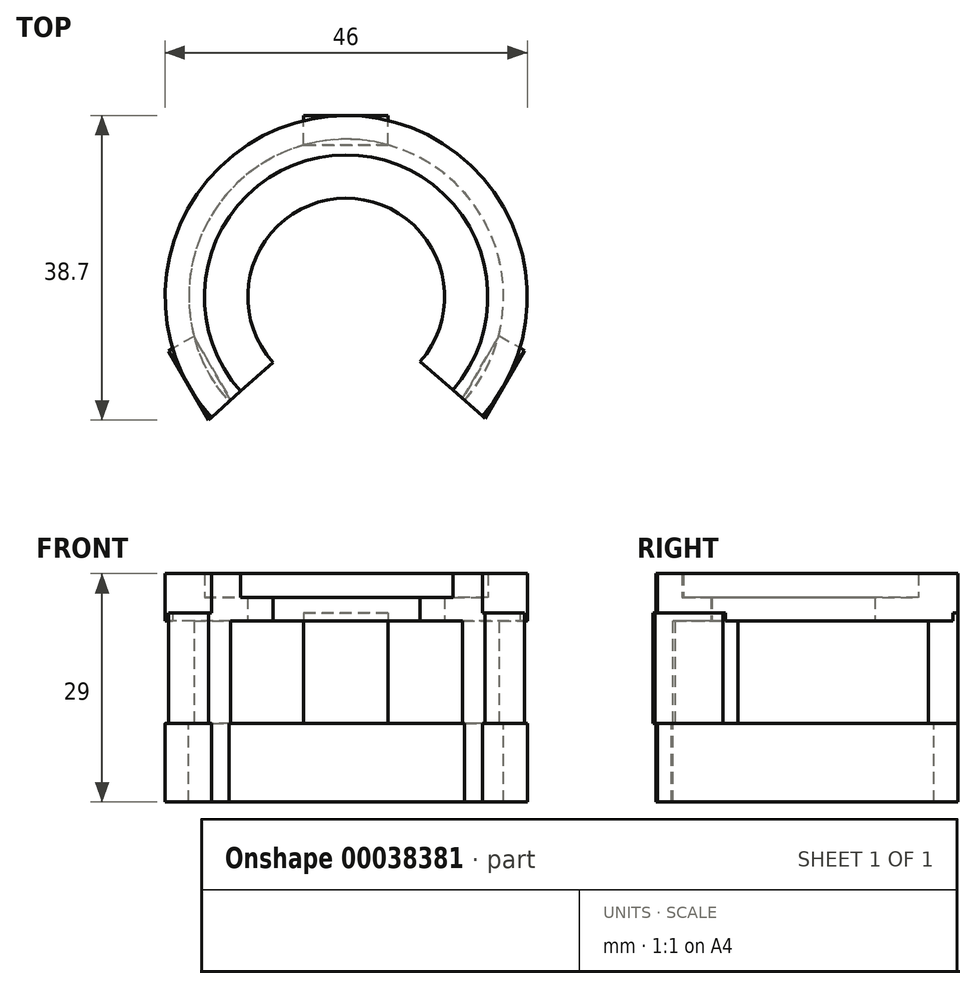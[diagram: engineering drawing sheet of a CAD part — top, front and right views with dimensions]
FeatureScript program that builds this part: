
annotation { "Feature Type Name" : "Feature", "Feature Type Description" : "" }
export const myFeature = defineFeature(function(context is Context, id is Id, definition is map)
    precondition{}
    {
        {
            var Q0;
            Q0=qCreatedBy(makeId("Top.planeOp"),FACE);
            var sketch = newSketch(context, id + "F0", { "sketchPlane" : qUnion([Q0])});
            skCircle(sketch, "E0", {"center": v(0, 0) * mm, "radius": 20 * mm});
            skCircle(sketch, "E1.0", {"center": v(0, 0) * mm, "radius": 23 * mm});
            skSolve(sketch);
        }
        {
            var Q0;
            Q0=makeQuery(id+"F0.imprint","IMPRINT",FACE,{"disambiguationData":[TD([[makeQuery(id+"F0.imprint","IMPRINT",EDGE,{"derivedFrom":sQuery(id+"F0.wireOp",EDGE,"E0")}),-1.0]])]});
            extrude(context, id + "F1", {"entities" : qUnion([Q0]), "oppositeDirection" : true, "depth" : 10 * mm});
        }
        {
            var Q0;
            Q0=qCreatedBy(makeId("Top.planeOp"),FACE);
            cPlane(context, id + "F2", {"entities" : qUnion([Q0]), "cplaneType" : CPlaneType.OFFSET, "offset" : 13 * mm, "width" : 150 * mm, "height" : 150 * mm});
        }
        {
            var Q0;
            Q0=qCreatedBy(id+"F2.planeOp",FACE);
            var sketch = newSketch(context, id + "F3", { "sketchPlane" : qUnion([Q0])});
            skCircle(sketch, "E2", {"center": v(0, 0) * mm, "radius": 18 * mm});
            skCircle(sketch, "E3", {"center": v(0, 0) * mm, "radius": 23 * mm});
            skSolve(sketch);
        }
        {
            var Q0;
            Q0=makeQuery(id+"F3.imprint","IMPRINT",FACE,{"disambiguationData":[TD([[makeQuery(id+"F3.imprint","IMPRINT",EDGE,{"derivedFrom":sQuery(id+"F3.wireOp",EDGE,"E2")}),-1.0]])]});
            extrude(context, id + "F4", {"entities" : qUnion([Q0]), "depth" : 6 * mm});
        }
        {
            var Q0;
            Q0=qCreatedBy(id+"F2.planeOp",FACE);
            var sketch = newSketch(context, id + "F5", { "sketchPlane" : qUnion([Q0])});
            skCircle(sketch, "E4", {"center": v(0, 0) * mm, "radius": 12.5 * mm});
            skCircle(sketch, "E5", {"center": v(0, 0) * mm, "radius": 23 * mm});
            skSolve(sketch);
        }
        {
            var Q0;
            Q0=makeQuery(id+"F5.imprint","IMPRINT",FACE,{"disambiguationData":[TD([[makeQuery(id+"F5.imprint","IMPRINT",EDGE,{"derivedFrom":sQuery(id+"F5.wireOp",EDGE,"E4")}),-1.0]])]});
            extrude(context, id + "F6", {"entities" : qUnion([Q0]), "depth" : 3 * mm});
        }
        {
            var Q0;
            Q0=qCreatedBy(makeId("Top.planeOp"),FACE);
            var sketch = newSketch(context, id + "F7", { "sketchPlane" : qUnion([Q0])});
            skLineSegment(sketch, "E6.bottom", {"start": v(-5.42, 23) * mm, "end": v(5.3, 23) * mm});
            skLineSegment(sketch, "E6.top", {"start": v(-5.42, 19.28) * mm, "end": v(5.3, 19.28) * mm});
            skLineSegment(sketch, "E6.left", {"start": v(-5.42, 23) * mm, "end": v(-5.42, 19.28) * mm});
            skLineSegment(sketch, "E6.right", {"start": v(5.3, 23) * mm, "end": v(5.3, 19.28) * mm});
            skLineSegment(sketch, "E7.1.0", {"start": v(-17.22, -16.2) * mm, "end": v(-14, -14.33) * mm});
            skLineSegment(sketch, "E7.1.1", {"start": v(-14, -14.33) * mm, "end": v(-19.36, -5.04) * mm});
            skLineSegment(sketch, "E7.1.2", {"start": v(-17.22, -16.2) * mm, "end": v(-22.58, -6.9) * mm});
            skLineSegment(sketch, "E7.1.3", {"start": v(-22.58, -6.9) * mm, "end": v(-19.36, -5.04) * mm});
            skLineSegment(sketch, "E7.2.0", {"start": v(22.64, -6.81) * mm, "end": v(19.4, -4.95) * mm});
            skLineSegment(sketch, "E7.2.1", {"start": v(19.4, -4.95) * mm, "end": v(14.05, -14.24) * mm});
            skLineSegment(sketch, "E7.2.2", {"start": v(22.64, -6.81) * mm, "end": v(17.27, -16.1) * mm});
            skLineSegment(sketch, "E7.2.3", {"start": v(17.27, -16.1) * mm, "end": v(14.05, -14.24) * mm});
            skPoint(sketch, "E7.center", {"position": v(0, 0) * mm});
            skSolve(sketch);
        }
        {
            var Q0;
            Q0 = qSketchRegion(id + "F7", true);
            extrude(context, id + "F8", {"entities" : qUnion([Q0]), "operationType" : NewBodyOperationType.ADD, "depth" : 14 * mm});
        }
        {
            var Q0;
            Q0=qCreatedBy(makeId("Top.planeOp"),FACE);
            var sketch = newSketch(context, id + "F9", { "sketchPlane" : qUnion([Q0])});
            skLineSegment(sketch, "E8", {"start": v(0, 0) * mm, "end": v(-19.2, -17.21) * mm});
            skLineSegment(sketch, "E9", {"start": v(-19.2, -17.21) * mm, "end": v(0.8, -30.17) * mm});
            skLineSegment(sketch, "E10", {"start": v(0.8, -30.17) * mm, "end": v(20.58, -18) * mm});
            skLineSegment(sketch, "E11", {"start": v(20.58, -18) * mm, "end": v(0, 0) * mm});
            skSolve(sketch);
        }
        {
            var Q0;
            Q0=makeQuery(id+"F9.imprint","IMPRINT",FACE,{"disambiguationData":[TD([[makeQuery(id+"F9.imprint","IMPRINT",EDGE,{"derivedFrom":sQuery(id+"F9.wireOp",EDGE,"E8")}),1.0]])]});
            extrude(context, id + "F10", {"entities" : qUnion([Q0]), "endBound" : BoundingType.SYMMETRIC, "depth" : 40 * mm});
        }
        {
            var Q0;
            Q0=makeQuery(id+"F10.opExtrude","SWEPT_BODY",BODY,{"disambiguationData":[OSD([sQuery(id+"F9.wireOp",EDGE,"E8"),sQuery(id+"F9.wireOp",EDGE,"E9"),sQuery(id+"F9.wireOp",EDGE,"E10"),sQuery(id+"F9.wireOp",EDGE,"E11")])]});
            var Q1;
            Q1=makeQuery(id+"F1.opExtrude","SWEPT_BODY",BODY,{"disambiguationData":[OSD([sQuery(id+"F0.wireOp",EDGE,"E0"),sQuery(id+"F0.wireOp",EDGE,"E1.0")])]});
            booleanBodies(context, id + "F11", {"operationType" : BooleanOperationType.SUBTRACTION, "tools" : qUnion([Q0]), "targets" : qUnion([Q1])});
        }
    });
